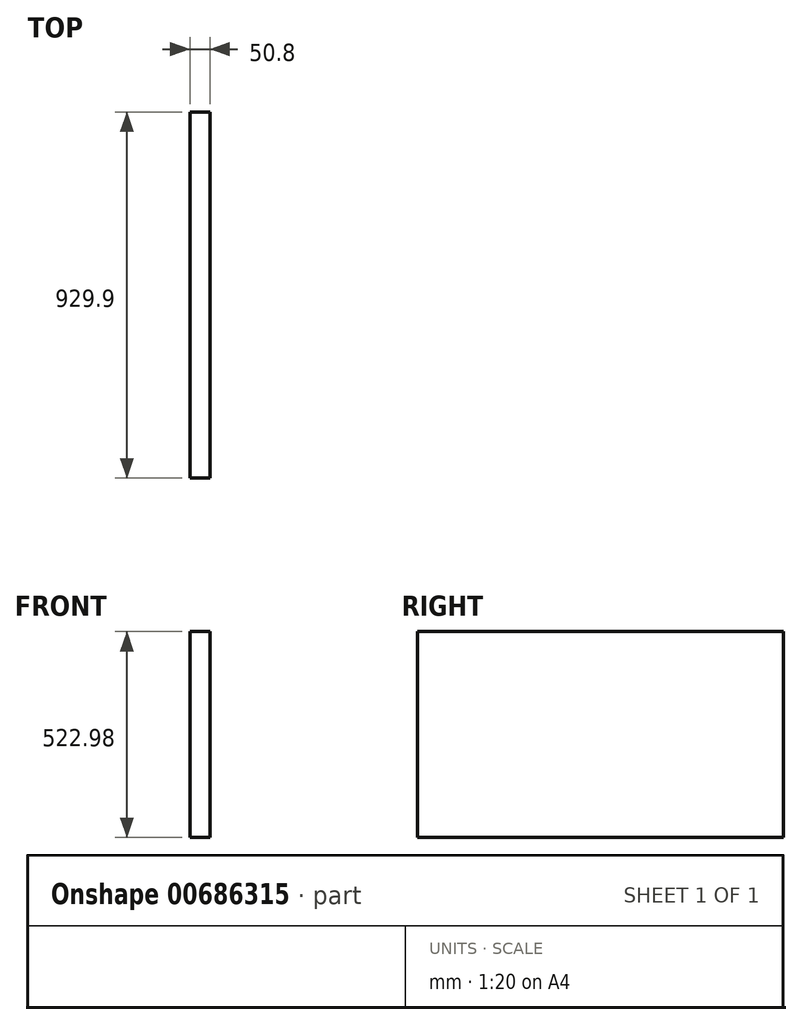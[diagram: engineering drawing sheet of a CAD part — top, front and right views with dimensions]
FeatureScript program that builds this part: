
annotation { "Feature Type Name" : "Feature", "Feature Type Description" : "" }
export const myFeature = defineFeature(function(context is Context, id is Id, definition is map)
    precondition{}
    {
        {
            var Q0;
            Q0=qCreatedBy(makeId("Right.planeOp"),FACE);
            var sketch = newSketch(context, id + "F0", { "sketchPlane" : qUnion([Q0])});
            skLineSegment(sketch, "E0.bottom", {"start": v(-464.95, 261.5) * mm, "end": v(464.95, 261.5) * mm});
            skLineSegment(sketch, "E0.top", {"start": v(-464.95, -261.5) * mm, "end": v(464.95, -261.5) * mm});
            skLineSegment(sketch, "E0.left", {"start": v(-464.95, 261.5) * mm, "end": v(-464.95, -261.5) * mm});
            skLineSegment(sketch, "E0.right", {"start": v(464.95, 261.5) * mm, "end": v(464.95, -261.5) * mm});
            skPoint(sketch, "E0.middle", {"position": v(0, 0) * mm});
            skSolve(sketch);
        }
        {
            var Q0;
            Q0=makeQuery(id+"F0.imprint","IMPRINT",FACE,{"disambiguationData":[TD([[makeQuery(id+"F0.imprint","IMPRINT",EDGE,{"derivedFrom":sQuery(id+"F0.wireOp",EDGE,"E0.bottom")}),-1.0]])]});
            extrude(context, id + "F1", {"entities" : qUnion([Q0]), "oppositeDirection" : true, "depth" : 50.8 * mm, "offsetDistance" : 25.4 * mm});
        }
    });
